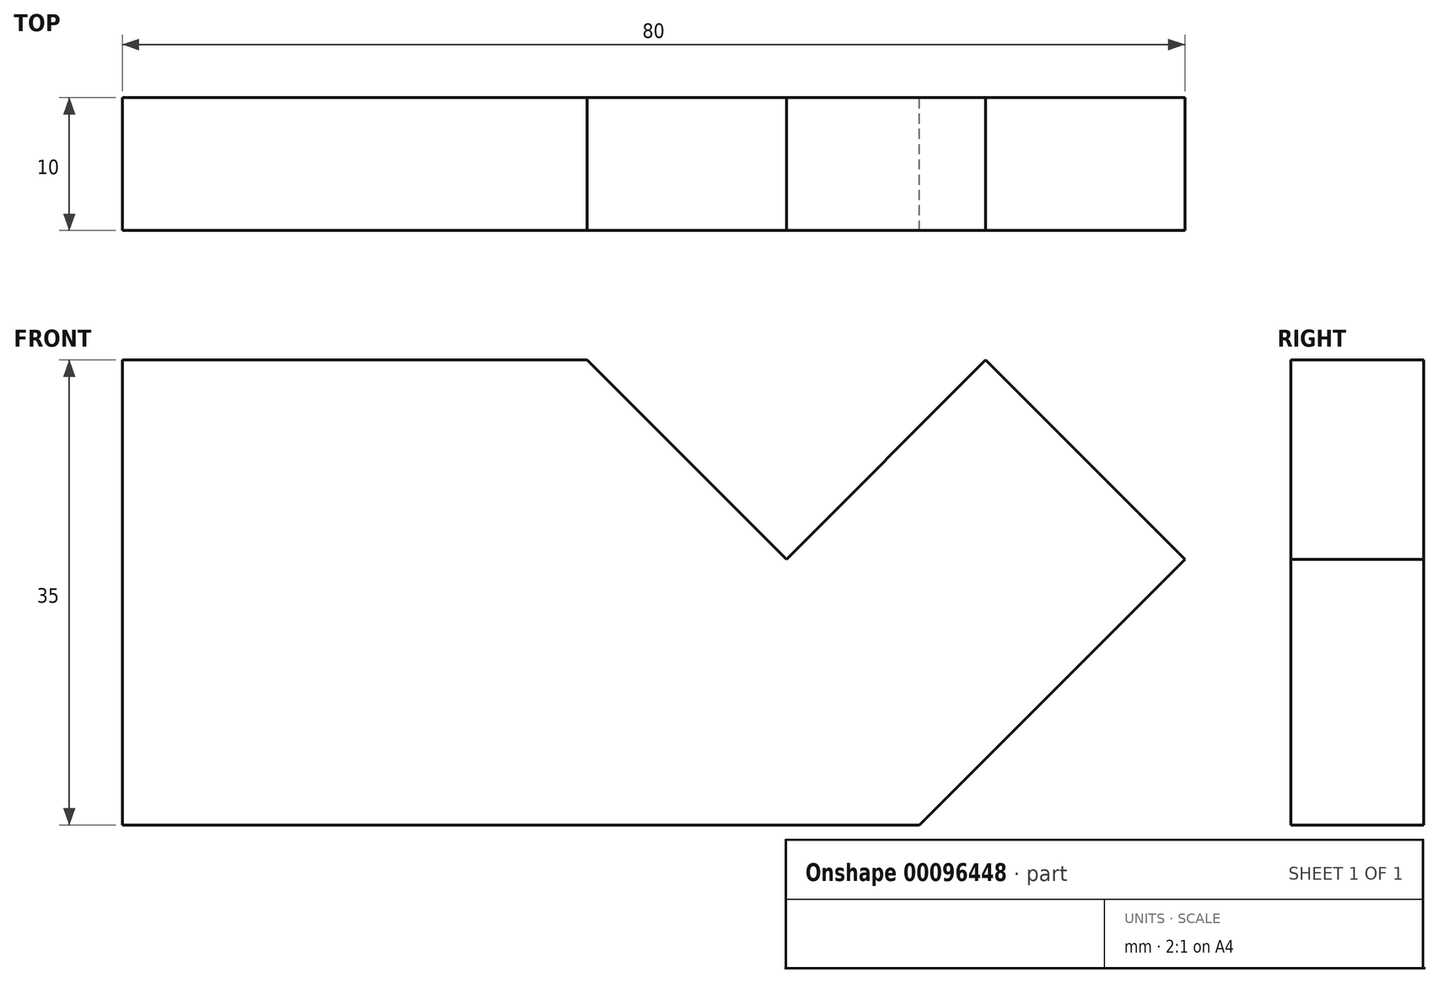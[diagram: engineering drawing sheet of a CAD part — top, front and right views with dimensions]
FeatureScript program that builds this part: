
annotation { "Feature Type Name" : "Feature", "Feature Type Description" : "" }
export const myFeature = defineFeature(function(context is Context, id is Id, definition is map)
    precondition{}
    {
        {
            var Q0;
            Q0=qCreatedBy(makeId("Front.planeOp"),FACE);
            var sketch = newSketch(context, id + "F0", { "sketchPlane" : qUnion([Q0])});
            skLineSegment(sketch, "E0", {"start": v(0, 0) * mm, "end": v(0, 35) * mm});
            skLineSegment(sketch, "E1", {"start": v(0, 35) * mm, "end": v(35, 35) * mm});
            skLineSegment(sketch, "E2", {"start": v(35, 35) * mm, "end": v(50, 20) * mm});
            skLineSegment(sketch, "E3", {"start": v(50, 20) * mm, "end": v(65, 35) * mm});
            skLineSegment(sketch, "E4", {"start": v(60, 0) * mm, "end": v(0, 0) * mm});
            skLineSegment(sketch, "E5", {"start": v(65, 35) * mm, "end": v(80, 20) * mm});
            skLineSegment(sketch, "E6", {"start": v(80, 20) * mm, "end": v(60, 0) * mm});
            skLineSegment(sketch, "E7", {"start": v(35, 35) * mm, "end": v(65, 35) * mm, "construction": true});
            skSolve(sketch);
        }
        {
            var Q0;
            Q0=makeQuery(id+"F0.imprint","IMPRINT",FACE,{"disambiguationData":[TD([[makeQuery(id+"F0.imprint","IMPRINT",EDGE,{"derivedFrom":sQuery(id+"F0.wireOp",EDGE,"E0")}),-1.0]])]});
            extrude(context, id + "F1", {"entities" : qUnion([Q0]), "depth" : 10 * mm});
        }
    });
